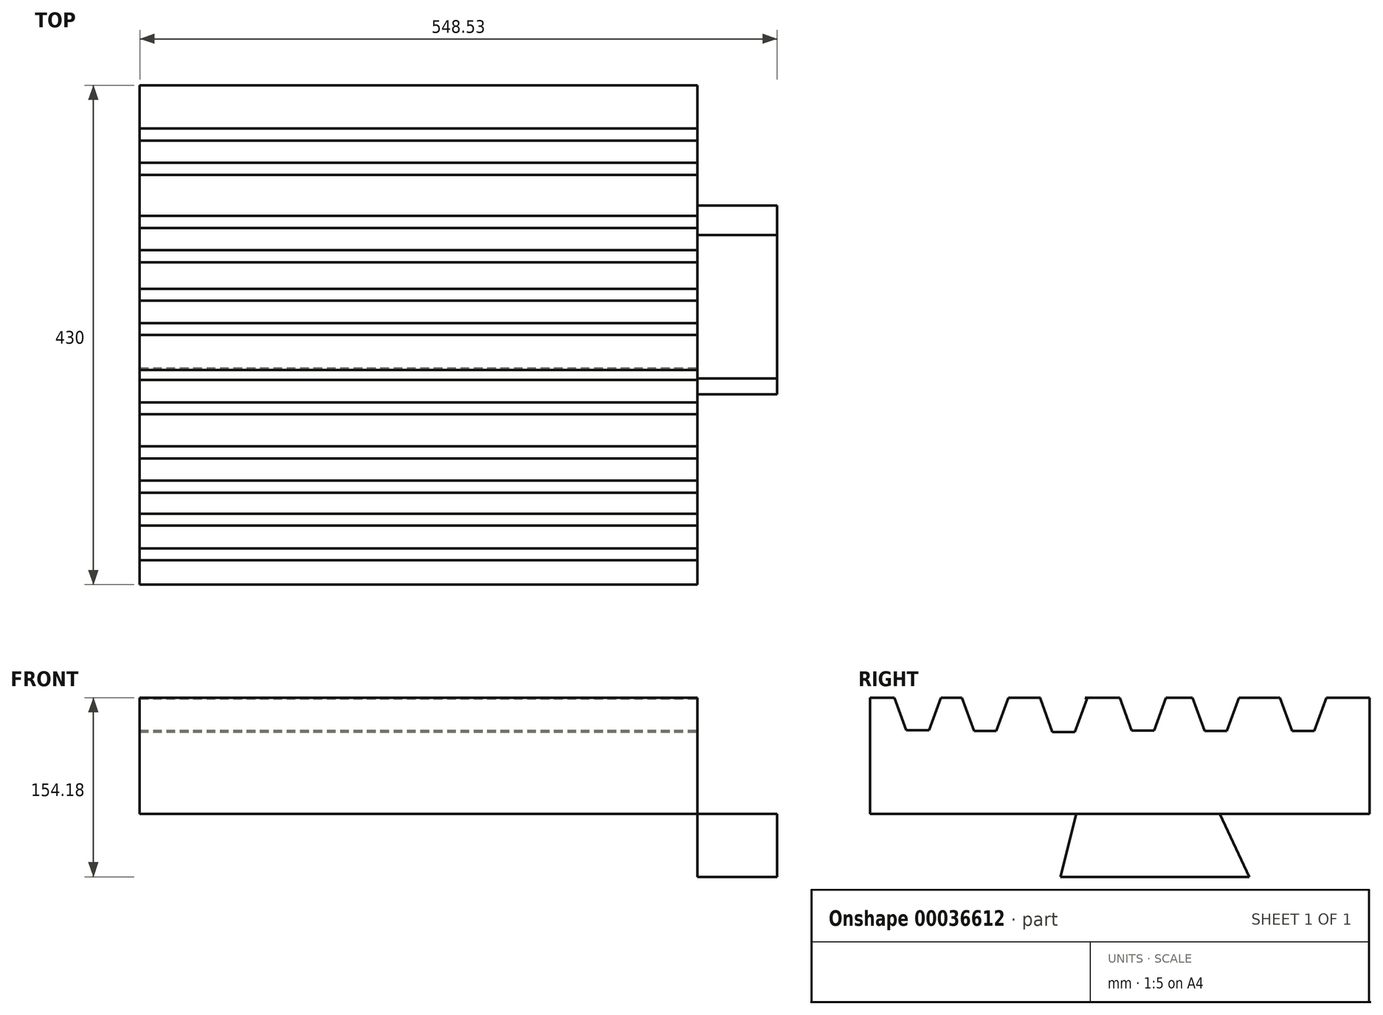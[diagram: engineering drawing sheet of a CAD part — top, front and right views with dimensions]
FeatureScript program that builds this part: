
annotation { "Feature Type Name" : "Feature", "Feature Type Description" : "" }
export const myFeature = defineFeature(function(context is Context, id is Id, definition is map)
    precondition{}
    {
        {
            var Q0;
            Q0=qCreatedBy(makeId("Top.planeOp"),FACE);
            var sketch = newSketch(context, id + "F0", { "sketchPlane" : qUnion([Q0])});
            skLineSegment(sketch, "E0.bottom", {"start": v(-218.48, 267.5) * mm, "end": v(211.52, 267.5) * mm});
            skLineSegment(sketch, "E0.top", {"start": v(-218.48, -162.5) * mm, "end": v(211.52, -162.5) * mm});
            skLineSegment(sketch, "E0.left", {"start": v(-218.48, 267.5) * mm, "end": v(-218.48, -162.5) * mm});
            skLineSegment(sketch, "E0.right", {"start": v(211.52, 267.5) * mm, "end": v(211.52, -162.5) * mm});
            skSolve(sketch);
        }
        {
            var Q0;
            Q0=makeQuery(id+"F0.imprint","IMPRINT",FACE,{"disambiguationData":[TD([[makeQuery(id+"F0.imprint","IMPRINT",EDGE,{"derivedFrom":sQuery(id+"F0.wireOp",EDGE,"E0.bottom")}),-1.0]])]});
            extrude(context, id + "F1", {"entities" : qUnion([Q0]), "depth" : 100 * mm});
        }
        {
            var Q0;
            Q0=makeQuery(id+"F1.opExtrude","SWEPT_FACE",FACE,{"disambiguationData":[OSD([sQuery(id+"F0.wireOp",EDGE,"E0.right")])]});
            var sketch = newSketch(context, id + "F2", { "sketchPlane" : qUnion([Q0])});
            skLineSegment(sketch, "E1", {"start": v(-141.58, 100) * mm, "end": v(-131.39, 72) * mm});
            skLineSegment(sketch, "E2", {"start": v(-131.39, 72) * mm, "end": v(-111.77, 72) * mm});
            skLineSegment(sketch, "E3", {"start": v(-111.77, 72) * mm, "end": v(-101.58, 100) * mm});
            skLineSegment(sketch, "E4", {"start": v(-101.58, 100) * mm, "end": v(-120.47, 111.35) * mm});
            skLineSegment(sketch, "E5", {"start": v(-120.47, 111.35) * mm, "end": v(-140.8, 108.77) * mm});
            skLineSegment(sketch, "E6", {"start": v(-140.8, 108.77) * mm, "end": v(-141.58, 100) * mm});
            skLineSegment(sketch, "E7", {"start": v(-43.39, 99.9) * mm, "end": v(-62.28, 111.26) * mm});
            skLineSegment(sketch, "E8", {"start": v(-72.97, 71.27) * mm, "end": v(-53.81, 71.27) * mm});
            skLineSegment(sketch, "E9", {"start": v(-53.81, 71.27) * mm, "end": v(-43.39, 99.9) * mm});
            skLineSegment(sketch, "E10", {"start": v(-83.39, 99.9) * mm, "end": v(-72.97, 71.27) * mm});
            skLineSegment(sketch, "E11", {"start": v(-62.28, 111.26) * mm, "end": v(-82.62, 108.68) * mm});
            skLineSegment(sketch, "E12", {"start": v(-82.62, 108.68) * mm, "end": v(-83.39, 99.9) * mm});
            skLineSegment(sketch, "E13", {"start": v(24.05, 99.02) * mm, "end": v(5.15, 110.37) * mm});
            skLineSegment(sketch, "E14", {"start": v(-5.53, 70.39) * mm, "end": v(13.62, 70.39) * mm});
            skLineSegment(sketch, "E15", {"start": v(13.62, 70.39) * mm, "end": v(24.05, 99.02) * mm});
            skLineSegment(sketch, "E16", {"start": v(-15.95, 99.02) * mm, "end": v(-5.53, 70.39) * mm});
            skLineSegment(sketch, "E17", {"start": v(5.15, 110.37) * mm, "end": v(-15.18, 107.8) * mm});
            skLineSegment(sketch, "E18", {"start": v(-15.18, 107.8) * mm, "end": v(-15.95, 99.02) * mm});
            skLineSegment(sketch, "E19", {"start": v(92.26, 100.3) * mm, "end": v(73.37, 111.65) * mm});
            skLineSegment(sketch, "E20", {"start": v(62.68, 71.67) * mm, "end": v(81.84, 71.67) * mm});
            skLineSegment(sketch, "E21", {"start": v(81.84, 71.67) * mm, "end": v(92.26, 100.3) * mm});
            skLineSegment(sketch, "E22", {"start": v(52.26, 100.3) * mm, "end": v(62.68, 71.67) * mm});
            skLineSegment(sketch, "E23", {"start": v(73.37, 111.65) * mm, "end": v(53.03, 109.08) * mm});
            skLineSegment(sketch, "E24", {"start": v(53.03, 109.08) * mm, "end": v(52.26, 100.3) * mm});
            skLineSegment(sketch, "E25", {"start": v(155.07, 100.05) * mm, "end": v(136.18, 111.4) * mm});
            skLineSegment(sketch, "E26", {"start": v(125.5, 71.41) * mm, "end": v(144.65, 71.41) * mm});
            skLineSegment(sketch, "E27", {"start": v(144.65, 71.41) * mm, "end": v(155.07, 100.05) * mm});
            skLineSegment(sketch, "E28", {"start": v(115.07, 100.05) * mm, "end": v(125.5, 71.41) * mm});
            skLineSegment(sketch, "E29", {"start": v(136.18, 111.4) * mm, "end": v(115.84, 108.82) * mm});
            skLineSegment(sketch, "E30", {"start": v(115.84, 108.82) * mm, "end": v(115.07, 100.05) * mm});
            skLineSegment(sketch, "E31", {"start": v(230.23, 100.05) * mm, "end": v(211.34, 111.4) * mm});
            skLineSegment(sketch, "E32", {"start": v(200.66, 71.41) * mm, "end": v(219.81, 71.41) * mm});
            skLineSegment(sketch, "E33", {"start": v(219.81, 71.41) * mm, "end": v(230.23, 100.05) * mm});
            skLineSegment(sketch, "E34", {"start": v(190.23, 100.05) * mm, "end": v(200.66, 71.41) * mm});
            skLineSegment(sketch, "E35", {"start": v(211.34, 111.4) * mm, "end": v(191, 108.82) * mm});
            skLineSegment(sketch, "E36", {"start": v(191, 108.82) * mm, "end": v(190.23, 100.05) * mm});
            skSolve(sketch);
        }
        {
            var Q0;
            Q0 = qSketchRegion(id + "F2", true);
            extrude(context, id + "F3", {"entities" : qUnion([Q0]), "operationType" : NewBodyOperationType.REMOVE, "endBound" : BoundingType.THROUGH_ALL, "oppositeDirection" : true, "depth" : 25 * mm});
        }
        {
            var Q0;
            Q0=makeQuery(id+"F1.opExtrude","SWEPT_FACE",FACE,{"disambiguationData":[OSD([sQuery(id+"F0.wireOp",EDGE,"E0.right")])]});
            var sketch = newSketch(context, id + "F4", { "sketchPlane" : qUnion([Q0])});
            skLineSegment(sketch, "E37", {"start": v(155.05, 100) * mm, "end": v(150.4, 147.97) * mm});
            skLineSegment(sketch, "E38", {"start": v(155.28, 153.45) * mm, "end": v(196.32, 154.33) * mm});
            skLineSegment(sketch, "E39", {"start": v(201.3, 148.21) * mm, "end": v(190.25, 100) * mm});
            skPoint(sketch, "E40.visualSharp", {"position": v(149.89, 153.33) * mm});
            skArc(sketch, "E40.filletArc", {"start": v(155.28, 153.45) * mm, "mid": v(151.65, 151.77) * mm, "end": v(150.4, 147.97) * mm});
            skPoint(sketch, "E41.visualSharp", {"position": v(202.73, 154.46) * mm});
            skArc(sketch, "E41.filletArc", {"start": v(201.3, 148.21) * mm, "mid": v(200.3, 152.48) * mm, "end": v(196.32, 154.33) * mm});
            skSolve(sketch);
        }
        {
            var Q0;
            Q0=makeQuery(id+"F1.opExtrude","SWEPT_FACE",FACE,{"disambiguationData":[OSD([sQuery(id+"F0.wireOp",EDGE,"E0.left")])]});
            extrude(context, id + "F5", {"entities" : qUnion([Q0]), "operationType" : NewBodyOperationType.ADD, "depth" : 25 * mm});
        }
        {
            var Q0;
            Q0=makeQuery(id+"F5.opExtrude","CAP_FACE",FACE,{"disambiguationData":[OSD([sQuery(id+"F0.wireOp",EDGE,"E0.left")])],"isStart":false});
            extrude(context, id + "F6", {"entities" : qUnion([Q0]), "operationType" : NewBodyOperationType.ADD, "depth" : 25 * mm});
        }
        {
            var Q0;
            Q0=makeQuery(id+"F6.opExtrude","CAP_FACE",FACE,{"disambiguationData":[OSD([sQuery(id+"F0.wireOp",EDGE,"E0.left")])],"isStart":false});
            extrude(context, id + "F7", {"entities" : qUnion([Q0]), "operationType" : NewBodyOperationType.REMOVE, "depth" : 39.35 * mm});
        }
        {
            var Q0;
            {var subQ0=sQuery(id+"F0.wireOp",EDGE,"E0.right");Q0=makeQuery(id+"F4.imprint","IMPRINT",FACE,{"disambiguationData":[TD([[makeQuery(id+"F4.imprint","IMPRINT",EDGE,{"derivedFrom":makeQuery(id+"F1.opExtrude","CAP_EDGE",EDGE,{"disambiguationData":[OSD([subQ0])],"isStart":true})}),-1.0]])]});}
            var sketch = newSketch(context, id + "F8", { "sketchPlane" : qUnion([Q0])});
            skLineSegment(sketch, "E42", {"start": v(0, -59.33) * mm, "end": v(58.57, 170.9) * mm});
            skLineSegment(sketch, "E43", {"start": v(58.57, 170.9) * mm, "end": v(163.88, -54.18) * mm});
            skLineSegment(sketch, "E44", {"start": v(163.88, -54.18) * mm, "end": v(1.3, -54.18) * mm});
            skSolve(sketch);
        }
        {
            var Q0;
            {var subQ5=sQuery(id+"F8.wireOp",EDGE,"E44");Q0=makeQuery(id+"F8.imprint","IMPRINT",FACE,{"disambiguationData":[TD([[makeQuery(id+"F8.imprint","IMPRINT",EDGE,{"derivedFrom":subQ5}),-1.0]])]});}
            extrude(context, id + "F9", {"entities" : qUnion([Q0]), "depth" : 68.53 * mm});
        }
    });
